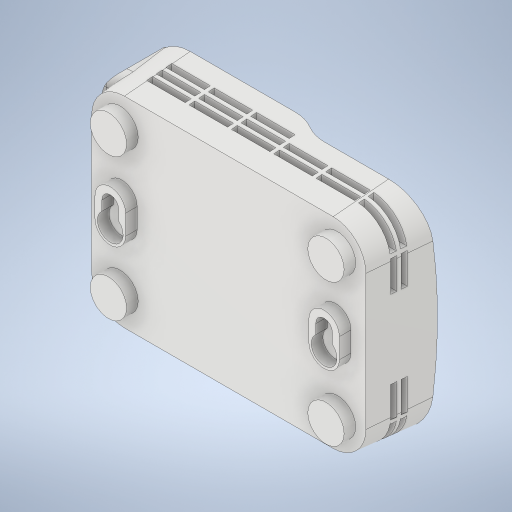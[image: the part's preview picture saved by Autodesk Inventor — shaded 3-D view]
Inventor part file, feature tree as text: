
AUTODESK INVENTOR PART (.ipt)
format: ipt  version: 2023.3 (Build 273359000, 359)  size: 836,608 bytes
history: native  units: in
note: dims shown in document units (in); Inventor stores cm internally (conversion verified against a paired STEP export)
features: projected_geometry x18, sketch x15, extrude x14, plane x6, fillet x1, pattern_linear x1
ambient origin geometry x8: Origin, YZ Plane, XZ Plane, XY Plane, X Axis, Y Axis, Z Axis, Center Point
bodies: Solid1 (feature_tree)
feature tree (55):
  extrude  "Extrusion1"  Depth=2.755in
  plane  "Work Plane2"
  extrude  "Extrusion2"  Depth=0.5in
  fillet  "Fillet1"  Radius=0.36in
  plane  "Work Plane3"
  extrude  "Extrusion3"  Depth=0.72in
  extrude  "Extrusion4"  Depth=0.5in
  extrude  "Extrusion5"  Depth=0.125in
  extrude  "Extrusion6"  Depth=0.04in
  plane  "Work Plane4"
  extrude  "Extrusion7"  Depth=0.13in
  plane  "Work Plane5"
  sketch  "Sketch11"  dims[d17=1.855in d18=0.0in d19=1.855in d20=0.0in]
  extrude  "Extrusion8"  Depth=1.855in TaperAngle=0.0deg
  plane  "Work Plane6"
  extrude  "Extrusion9"  Depth=1.855in TaperAngle=0.0deg
  extrude  "Extrusion10"  Depth=0.5in
  pattern_linear  "Rectangular Pattern1"  Count1=3 Spacing1=0.125in
  extrude  "Extrusion11"  Depth=0.295in
  extrude  "Extrusion12"  Depth=0.5in TaperAngle=0.0deg
  plane  "Work Plane7"
  extrude  "Extrusion13"  Depth=0.5425in TaperAngle=0.0deg
  extrude  "Extrusion14"  Depth=0.001in
  sketch  "Sketch1"  dims[d0=3.71in d1=2.755in]
  sketch  "Sketch4"  dims[d2=0.5in d3=0.855in d4=-0.0344in d5=0.36in]
  sketch  "Sketch5"  dims[d6=0.72in d7=0.72in]
  sketch  "Sketch6"  dims[d8=1.855in d9=0.0in d10=0.5in]
  projected_geometry  "Projected Loop1"
  sketch  "Sketch7"  dims[d11=-1.86in d12=0.125in]
  projected_geometry  "Projected Loop2"
  sketch  "Sketch8"  dims[d13=0.04in d14=0.65in]
  projected_geometry  "Projected Loop3"
  sketch  "Sketch9"  dims[d15=0.13in d16=0.13in]
  sketch  "Sketch12"  dims[d21=1.855in d22=0.0in d23=1.855in d24=0.0in]
  projected_geometry  "Projected Loop4"
  projected_geometry  "Projected Loop5"
  projected_geometry  "Projected Loop6"
  projected_geometry  "Projected Loop7"
  projected_geometry  "Projected Loop8"
  projected_geometry  "Projected Loop9"
  projected_geometry  "Projected Loop10"
  projected_geometry  "Projected Loop11"
  projected_geometry  "Projected Loop12"
  projected_geometry  "Projected Loop13"
  projected_geometry  "Projected Loop14"
  projected_geometry  "Projected Loop15"
  projected_geometry  "Projected Loop16"
  projected_geometry  "Projected Loop17"
  projected_geometry  "Projected Loop18"
  sketch  "Sketch13"  dims[d25=1.5in d26=0.5in]
  sketch  "Sketch14"  dims[d27=0.075in d28=1.1811in d30=0.125in d31=1.1811in d33=0.55in]
  sketch  "Sketch15"  dims[d36=1.5748in d38=0.55in d39=0.7874in d41=0.125in d44=0.295in]
  sketch  "Sketch16"  dims[d45=0.5in d46=0.5425in d47=0.0in]
  sketch  "Sketch17"  dims[d48=-1.375in d49=0.5425in d50=0.0in]
  sketch  "Sketch18"  dims[d51=1.875in d52=0.4in d53=0.4in d54=0.05in d55=0.05in d56=0.1675in d57=0.0in d59=0.436in d60=0.272in d61=0.325in d62=0.472in d63=0.07in d64=0.1675in d65=0.0in d66=0.03in d67=0.03in d68=0.7874in d70=0.6in d71=0.35in d72=0.45in d73=0.02in d74=0.0in d75=0.145in d76=0.0in d77=0.15in d78=0.26in d79=0.335in d80=0.216in d81=0.145in d82=0.0in d83=0.472in d84=0.001in d85=0.0in]
